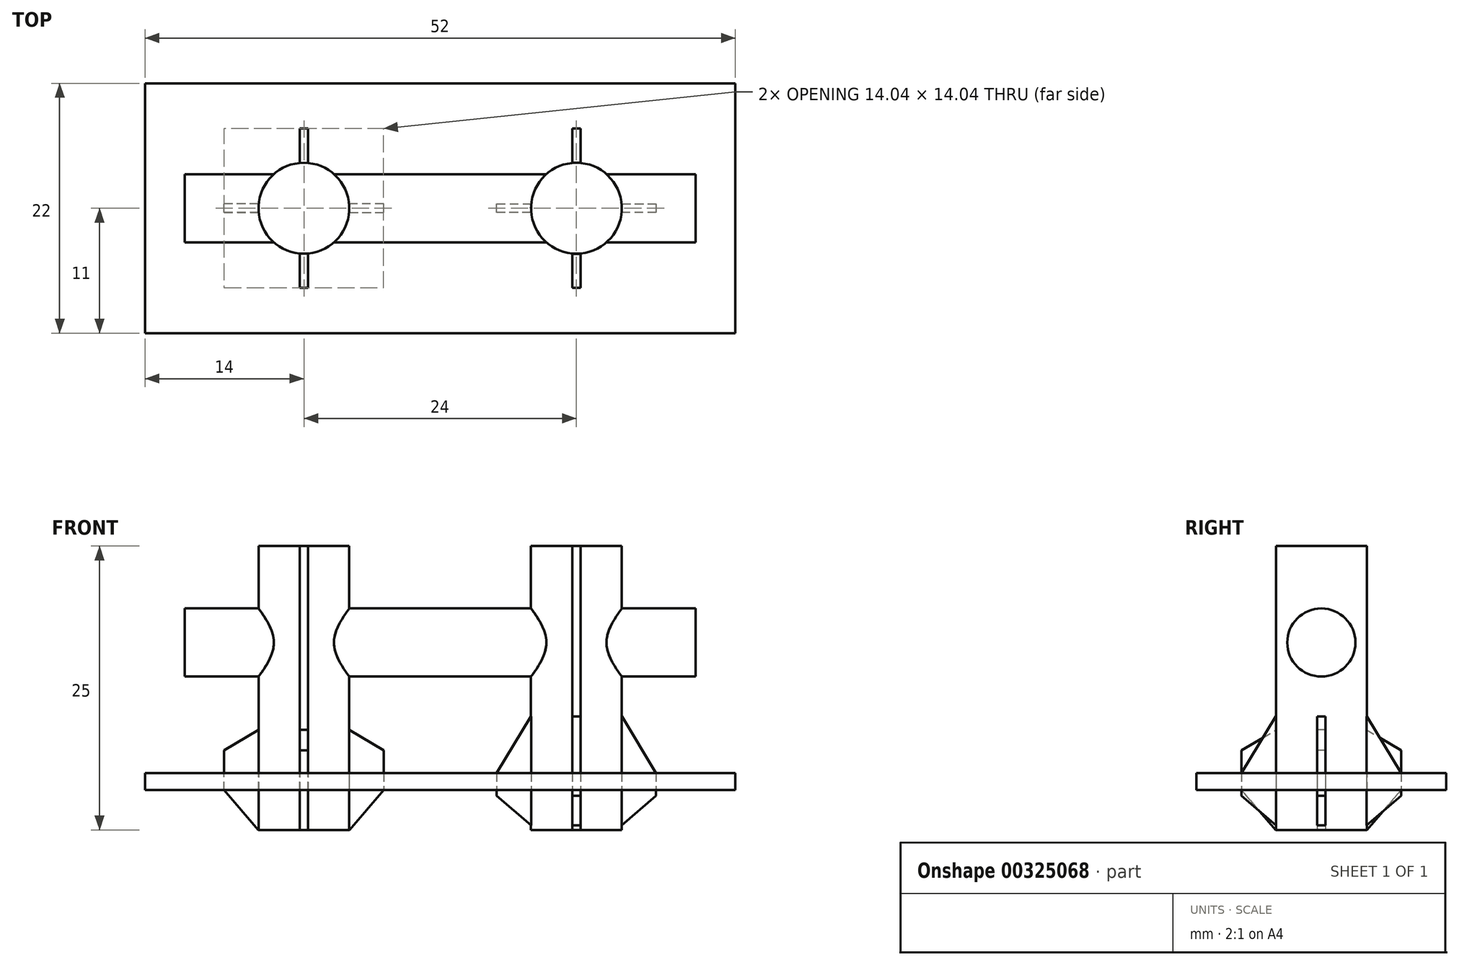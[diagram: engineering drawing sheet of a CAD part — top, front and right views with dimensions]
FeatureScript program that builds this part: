
annotation { "Feature Type Name" : "Feature", "Feature Type Description" : "" }
export const myFeature = defineFeature(function(context is Context, id is Id, definition is map)
    precondition{}
    {
        {
            var Q0;
            Q0=qCreatedBy(makeId("Top.planeOp"),FACE);
            var sketch = newSketch(context, id + "F0", { "sketchPlane" : qUnion([Q0])});
            skLineSegment(sketch, "E0.bottom", {"start": v(-26, 11) * mm, "end": v(26, 11) * mm});
            skLineSegment(sketch, "E0.top", {"start": v(-26, -11) * mm, "end": v(26, -11) * mm});
            skLineSegment(sketch, "E0.left", {"start": v(-26, 11) * mm, "end": v(-26, -11) * mm});
            skLineSegment(sketch, "E0.right", {"start": v(26, 11) * mm, "end": v(26, -11) * mm});
            skPoint(sketch, "E0.middle", {"position": v(0, 0) * mm});
            skLineSegment(sketch, "E1", {"start": v(0, 0) * mm, "end": v(-12, 0) * mm});
            skLineSegment(sketch, "E2", {"start": v(0, 0) * mm, "end": v(12, 0) * mm});
            skCircle(sketch, "E3", {"center": v(-12, 0) * mm, "radius": 4 * mm});
            skCircle(sketch, "E4", {"center": v(12, 0) * mm, "radius": 4 * mm});
            skLineSegment(sketch, "E5", {"start": v(12, -4) * mm, "end": v(12, -5.5) * mm});
            skLineSegment(sketch, "E6.bottom", {"start": v(11.62, -3.98) * mm, "end": v(12.38, -3.98) * mm});
            skLineSegment(sketch, "E6.top", {"start": v(11.63, -7.02) * mm, "end": v(12.38, -7.02) * mm});
            skLineSegment(sketch, "E6.left", {"start": v(11.63, -3.98) * mm, "end": v(11.63, -7.02) * mm});
            skLineSegment(sketch, "E6.right", {"start": v(12.38, -3.98) * mm, "end": v(12.38, -7.02) * mm});
            skPoint(sketch, "E6.middle", {"position": v(12, -5.5) * mm});
            skLineSegment(sketch, "E7", {"start": v(-12, -4) * mm, "end": v(-12, -5.5) * mm});
            skLineSegment(sketch, "E8.bottom", {"start": v(-11.62, -3.98) * mm, "end": v(-12.38, -3.98) * mm});
            skLineSegment(sketch, "E8.top", {"start": v(-11.62, -7.02) * mm, "end": v(-12.37, -7.02) * mm});
            skLineSegment(sketch, "E8.left", {"start": v(-11.62, -3.98) * mm, "end": v(-11.62, -7.02) * mm});
            skLineSegment(sketch, "E8.right", {"start": v(-12.38, -3.98) * mm, "end": v(-12.38, -7.02) * mm});
            skPoint(sketch, "E8.middle", {"position": v(-12, -5.5) * mm});
            skLineSegment(sketch, "E9.1.0", {"start": v(-15.98, 0.38) * mm, "end": v(-19.02, 0.38) * mm});
            skLineSegment(sketch, "E9.1.1", {"start": v(-15.98, -0.38) * mm, "end": v(-19.02, -0.38) * mm});
            skLineSegment(sketch, "E9.1.2", {"start": v(-19.02, -0.38) * mm, "end": v(-19.02, 0.37) * mm});
            skLineSegment(sketch, "E9.2.0", {"start": v(-11.62, 3.98) * mm, "end": v(-11.62, 7.02) * mm});
            skLineSegment(sketch, "E9.2.1", {"start": v(-12.38, 3.98) * mm, "end": v(-12.38, 7.02) * mm});
            skLineSegment(sketch, "E9.2.2", {"start": v(-12.38, 7.02) * mm, "end": v(-11.63, 7.02) * mm});
            skLineSegment(sketch, "E9.3.0", {"start": v(-8.02, -0.37) * mm, "end": v(-4.98, -0.37) * mm});
            skLineSegment(sketch, "E9.3.1", {"start": v(-8.02, 0.38) * mm, "end": v(-4.98, 0.38) * mm});
            skLineSegment(sketch, "E9.3.2", {"start": v(-4.98, 0.38) * mm, "end": v(-4.98, -0.37) * mm});
            skLineSegment(sketch, "E9.anchor1", {"start": v(-12, 0) * mm, "end": v(-12.38, -7.02) * mm, "construction": true});
            skLineSegment(sketch, "E9.anchor2", {"start": v(-12, 0) * mm, "end": v(-4.98, -0.37) * mm, "construction": true});
            skLineSegment(sketch, "E10.1.0", {"start": v(15.98, 0.38) * mm, "end": v(19.02, 0.38) * mm});
            skLineSegment(sketch, "E10.1.1", {"start": v(15.98, -0.37) * mm, "end": v(19.02, -0.37) * mm});
            skLineSegment(sketch, "E10.1.2", {"start": v(19.02, -0.37) * mm, "end": v(19.02, 0.38) * mm});
            skLineSegment(sketch, "E10.2.0", {"start": v(11.62, 3.98) * mm, "end": v(11.62, 7.02) * mm});
            skLineSegment(sketch, "E10.2.1", {"start": v(12.37, 3.98) * mm, "end": v(12.37, 7.02) * mm});
            skLineSegment(sketch, "E10.2.2", {"start": v(12.37, 7.02) * mm, "end": v(11.62, 7.02) * mm});
            skLineSegment(sketch, "E10.3.0", {"start": v(8.02, -0.37) * mm, "end": v(4.98, -0.37) * mm});
            skLineSegment(sketch, "E10.3.1", {"start": v(8.02, 0.38) * mm, "end": v(4.98, 0.38) * mm});
            skLineSegment(sketch, "E10.3.2", {"start": v(4.98, 0.38) * mm, "end": v(4.98, -0.38) * mm});
            skSolve(sketch);
        }
        {
            var Q0;
            Q0 = qSketchRegion(id + "F0", true);
            extrude(context, id + "F1", {"entities" : qUnion([Q0]), "oppositeDirection" : true, "depth" : 1.5 * mm, "offsetDistance" : 25 * mm});
        }
        {
            var Q0;
            {var subQ4=sQuery(id+"F0.wireOp",EDGE,"E8.bottom");Q0=makeQuery(id+"F0.imprint","IMPRINT",FACE,{"disambiguationData":[TD([[makeQuery(id+"F0.imprint","IMPRINT",EDGE,{"derivedFrom":subQ4}),-1.0]])]});}
            var Q1;
            {var subQ7=sQuery(id+"F0.wireOp",EDGE,"E6.bottom");Q1=makeQuery(id+"F0.imprint","IMPRINT",FACE,{"disambiguationData":[TD([[makeQuery(id+"F0.imprint","IMPRINT",EDGE,{"derivedFrom":subQ7}),1.0]])]});}
            extrude(context, id + "F2", {"entities" : qUnion([Q0, Q1]), "operationType" : NewBodyOperationType.ADD, "depth" : 20 * mm, "offsetDistance" : 25 * mm, "hasSecondDirection" : true, "secondDirectionOppositeDirection" : true, "secondDirectionDepth" : 5 * mm});
        }
        {
            var Q0;
            {var subQ0=sQuery(id+"F0.wireOp",EDGE,"E9.2.0");Q0=makeQuery(id+"F0.imprint","IMPRINT",FACE,{"disambiguationData":[TD([[makeQuery(id+"F0.imprint","IMPRINT",EDGE,{"derivedFrom":subQ0}),1.0]])]});}
            var Q1;
            {var subQ5=sQuery(id+"F0.wireOp",EDGE,"E9.3.1");Q1=makeQuery(id+"F0.imprint","IMPRINT",FACE,{"disambiguationData":[TD([[makeQuery(id+"F0.imprint","IMPRINT",EDGE,{"derivedFrom":subQ5}),-1.0]])]});}
            var Q2;
            {var subQ5=sQuery(id+"F0.wireOp",EDGE,"E9.3.0");Q2=makeQuery(id+"F0.imprint","IMPRINT",FACE,{"disambiguationData":[TD([[makeQuery(id+"F0.imprint","IMPRINT",EDGE,{"derivedFrom":subQ5}),1.0]])]});}
            var Q3;
            Q3=makeQuery(id+"F0.imprint","IMPRINT",FACE,{"disambiguationData":[TD([[makeQuery(id+"F0.imprint","IMPRINT",EDGE,{"derivedFrom":sQuery(id+"F0.wireOp",EDGE,"E8.top")}),-1.0]])]});
            var Q4;
            {var subQ0=sQuery(id+"F0.wireOp",EDGE,"E9.1.0");Q4=makeQuery(id+"F0.imprint","IMPRINT",FACE,{"disambiguationData":[TD([[makeQuery(id+"F0.imprint","IMPRINT",EDGE,{"derivedFrom":subQ0}),1.0]])]});}
            var Q5;
            {var subQ5=sQuery(id+"F0.wireOp",EDGE,"E10.3.1");Q5=makeQuery(id+"F0.imprint","IMPRINT",FACE,{"disambiguationData":[TD([[makeQuery(id+"F0.imprint","IMPRINT",EDGE,{"derivedFrom":subQ5}),1.0]])]});}
            var Q6;
            {var subQ5=sQuery(id+"F0.wireOp",EDGE,"E10.3.0");Q6=makeQuery(id+"F0.imprint","IMPRINT",FACE,{"disambiguationData":[TD([[makeQuery(id+"F0.imprint","IMPRINT",EDGE,{"derivedFrom":subQ5}),-1.0]])]});}
            var Q7;
            Q7=makeQuery(id+"F0.imprint","IMPRINT",FACE,{"disambiguationData":[TD([[makeQuery(id+"F0.imprint","IMPRINT",EDGE,{"derivedFrom":sQuery(id+"F0.wireOp",EDGE,"E6.top")}),1.0]])]});
            var Q8;
            {var subQ0=sQuery(id+"F0.wireOp",EDGE,"E10.1.0");Q8=makeQuery(id+"F0.imprint","IMPRINT",FACE,{"disambiguationData":[TD([[makeQuery(id+"F0.imprint","IMPRINT",EDGE,{"derivedFrom":subQ0}),-1.0]])]});}
            var Q9;
            {var subQ0=sQuery(id+"F0.wireOp",EDGE,"E10.2.0");Q9=makeQuery(id+"F0.imprint","IMPRINT",FACE,{"disambiguationData":[TD([[makeQuery(id+"F0.imprint","IMPRINT",EDGE,{"derivedFrom":subQ0}),-1.0]])]});}
            extrude(context, id + "F3", {"entities" : qUnion([Q0, Q1, Q2, Q3, Q4, Q5, Q6, Q7, Q8, Q9]), "depth" : 5 * mm, "offsetDistance" : 25 * mm, "hasSecondDirection" : true, "secondDirectionOppositeDirection" : true, "secondDirectionDepth" : 5 * mm});
        }
        {
            var Q0;
            Q0=makeQuery(id+"F3.opExtrude","CAP_EDGE",EDGE,{"disambiguationData":[OSD([sQuery(id+"F0.wireOp",EDGE,"E8.top")])],"isStart":false});
            var Q1;
            Q1=makeQuery(id+"F3.opExtrude","CAP_EDGE",EDGE,{"disambiguationData":[OSD([sQuery(id+"F0.wireOp",EDGE,"E9.3.2")])],"isStart":false});
            var Q2;
            Q2=makeQuery(id+"F3.opExtrude","CAP_EDGE",EDGE,{"disambiguationData":[OSD([sQuery(id+"F0.wireOp",EDGE,"E9.1.2")])],"isStart":false});
            var Q3;
            Q3=makeQuery(id+"F3.opExtrude","CAP_EDGE",EDGE,{"disambiguationData":[OSD([sQuery(id+"F0.wireOp",EDGE,"E9.2.2")])],"isStart":false});
            chamfer(context, id + "F4", {"entities" : qUnion([Q0, Q1, Q2, Q3]), "chamferType" : ChamferType.TWO_OFFSETS, "width1" : 5 * mm, "oppositeDirection" : false, "width2" : 3 * mm, "tangentPropagation" : true});
        }
        {
            var Q0;
            Q0=makeQuery(id+"F3.opExtrude","CAP_EDGE",EDGE,{"disambiguationData":[OSD([sQuery(id+"F0.wireOp",EDGE,"E9.2.2")])],"isStart":true});
            var Q1;
            Q1=makeQuery(id+"F3.opExtrude","CAP_EDGE",EDGE,{"disambiguationData":[OSD([sQuery(id+"F0.wireOp",EDGE,"E9.1.2")])],"isStart":true});
            var Q2;
            Q2=makeQuery(id+"F3.opExtrude","CAP_EDGE",EDGE,{"disambiguationData":[OSD([sQuery(id+"F0.wireOp",EDGE,"E8.top")])],"isStart":true});
            var Q3;
            Q3=makeQuery(id+"F3.opExtrude","CAP_EDGE",EDGE,{"disambiguationData":[OSD([sQuery(id+"F0.wireOp",EDGE,"E9.3.2")])],"isStart":true});
            chamfer(context, id + "F5", {"entities" : qUnion([Q0, Q1, Q2, Q3]), "chamferType" : ChamferType.TWO_OFFSETS, "width1" : 3 * mm, "oppositeDirection" : false, "width2" : 3.5 * mm, "tangentPropagation" : true});
        }
        {
            var Q0;
            Q0=makeQuery(id+"F3.opExtrude","CAP_EDGE",EDGE,{"disambiguationData":[OSD([sQuery(id+"F0.wireOp",EDGE,"E10.1.2")])],"isStart":true});
            var Q1;
            Q1=makeQuery(id+"F3.opExtrude","CAP_EDGE",EDGE,{"disambiguationData":[OSD([sQuery(id+"F0.wireOp",EDGE,"E10.2.2")])],"isStart":true});
            var Q2;
            Q2=makeQuery(id+"F3.opExtrude","CAP_EDGE",EDGE,{"disambiguationData":[OSD([sQuery(id+"F0.wireOp",EDGE,"E10.3.2")])],"isStart":true});
            var Q3;
            Q3=makeQuery(id+"F3.opExtrude","CAP_EDGE",EDGE,{"disambiguationData":[OSD([sQuery(id+"F0.wireOp",EDGE,"E6.top")])],"isStart":true});
            chamfer(context, id + "F6", {"entities" : qUnion([Q0, Q1, Q2, Q3]), "chamferType" : ChamferType.TWO_OFFSETS, "width1" : 3.5 * mm, "oppositeDirection" : false, "width2" : 3 * mm, "tangentPropagation" : true});
        }
        {
            var Q0;
            Q0=makeQuery(id+"F3.opExtrude","CAP_EDGE",EDGE,{"disambiguationData":[OSD([sQuery(id+"F0.wireOp",EDGE,"E6.top")])],"isStart":false});
            var Q1;
            Q1=makeQuery(id+"F3.opExtrude","CAP_EDGE",EDGE,{"disambiguationData":[OSD([sQuery(id+"F0.wireOp",EDGE,"E10.3.2")])],"isStart":false});
            var Q2;
            Q2=makeQuery(id+"F3.opExtrude","CAP_EDGE",EDGE,{"disambiguationData":[OSD([sQuery(id+"F0.wireOp",EDGE,"E10.1.2")])],"isStart":false});
            var Q3;
            Q3=makeQuery(id+"F3.opExtrude","CAP_EDGE",EDGE,{"disambiguationData":[OSD([sQuery(id+"F0.wireOp",EDGE,"E10.2.2")])],"isStart":false});
            chamfer(context, id + "F7", {"entities" : qUnion([Q0, Q1, Q2, Q3]), "chamferType" : ChamferType.TWO_OFFSETS, "width1" : 3 * mm, "oppositeDirection" : false, "width2" : 5 * mm, "tangentPropagation" : true});
        }
        {
            var Q0;
            Q0=qCreatedBy(makeId("Right.planeOp"),FACE);
            var sketch = newSketch(context, id + "F8", { "sketchPlane" : qUnion([Q0])});
            skCircle(sketch, "E11", {"center": v(0, 11.5) * mm, "radius": 3 * mm});
            skSolve(sketch);
        }
        {
            var Q0;
            Q0=makeQuery(id+"F8.imprint","IMPRINT",FACE,{"disambiguationData":[TD([[makeQuery(id+"F8.imprint","IMPRINT",EDGE,{"derivedFrom":sQuery(id+"F8.wireOp",EDGE,"E11")}),1.0]])]});
            extrude(context, id + "F9", {"entities" : qUnion([Q0]), "operationType" : NewBodyOperationType.ADD, "depth" : 45 * mm, "offsetDistance" : 25 * mm, "symmetric" : true});
        }
    });
